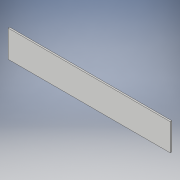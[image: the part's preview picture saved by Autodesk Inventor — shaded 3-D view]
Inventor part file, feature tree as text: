
AUTODESK INVENTOR PART (.ipt)
format: ipt  version: 2017 (Build 210142000, 142)  size: 90,112 bytes
history: native  units: in
note: dims shown in document units (in); Inventor stores cm internally (conversion verified against a paired STEP export)
features: extrude x1, sketch x1
ambient origin geometry x8: Origin, YZ Plane, XZ Plane, XY Plane, X Axis, Y Axis, Z Axis, Center Point
bodies: Solid1 (feature_tree)
feature tree (2):
  extrude  "Extrusion1"  Depth=12.0in
  sketch  "Sketch1"  dims[d0=72.0in d1=12.0in d2=0.7188in d3=0.0in]
